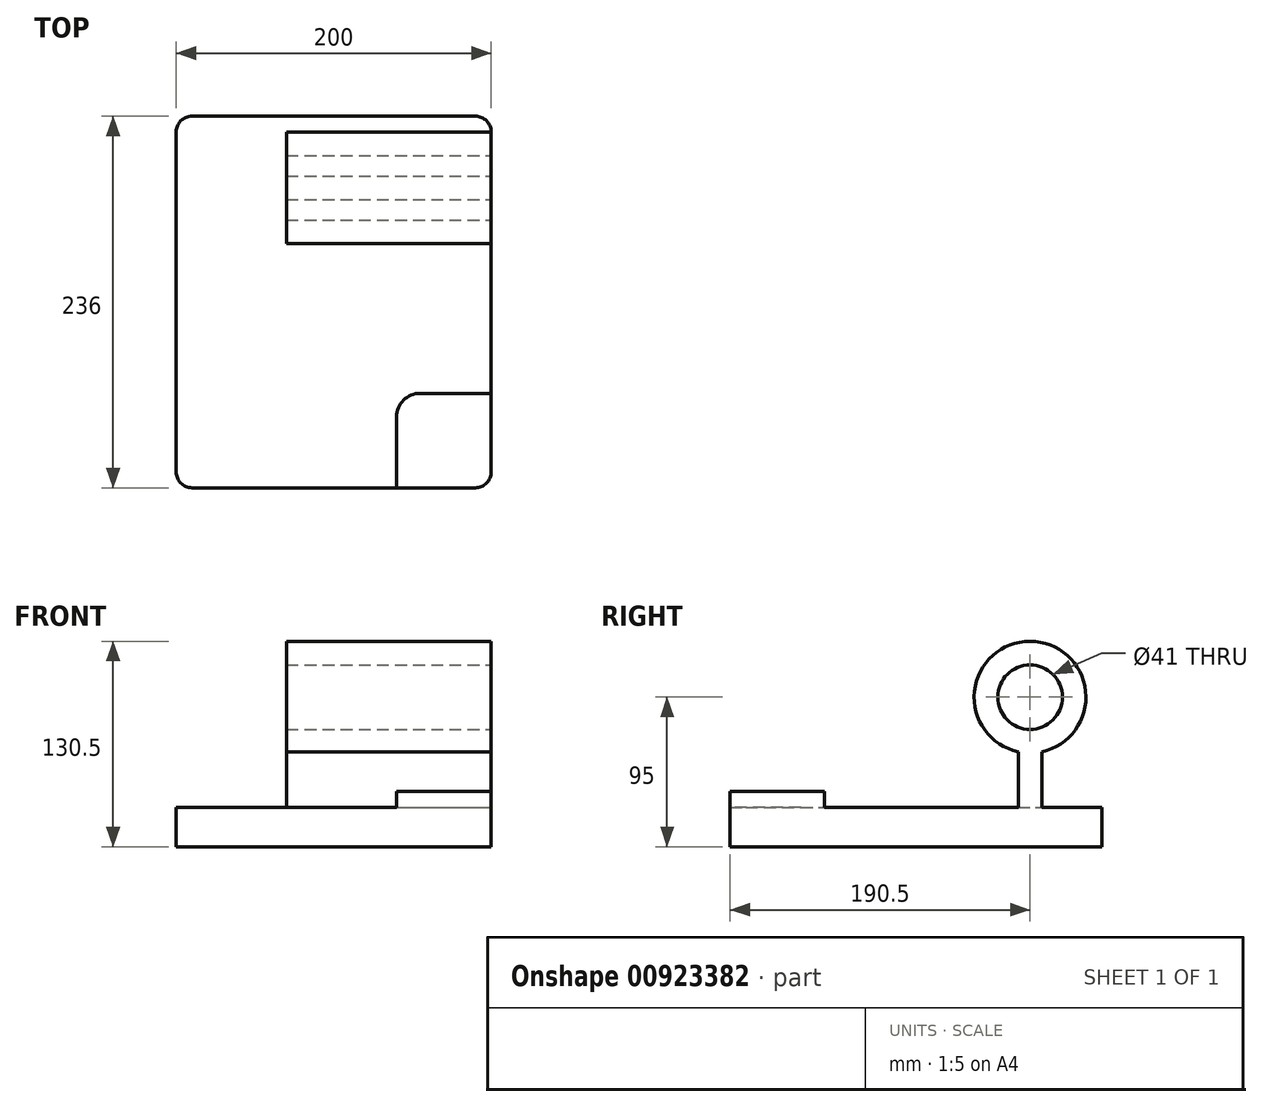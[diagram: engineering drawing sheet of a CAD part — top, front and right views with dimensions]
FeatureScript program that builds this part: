
annotation { "Feature Type Name" : "Feature", "Feature Type Description" : "" }
export const myFeature = defineFeature(function(context is Context, id is Id, definition is map)
    precondition{}
    {
        {
            var Q0;
            Q0=qCreatedBy(makeId("Right.planeOp"),FACE);
            var sketch = newSketch(context, id + "F0", { "sketchPlane" : qUnion([Q0])});
            skLineSegment(sketch, "E0", {"start": v(0, 0) * mm, "end": v(60, 0) * mm});
            skLineSegment(sketch, "E1", {"start": v(60, 0) * mm, "end": v(60, -10) * mm});
            skLineSegment(sketch, "E2", {"start": v(60, -10) * mm, "end": v(183, -10) * mm});
            skLineSegment(sketch, "E3", {"start": v(183, -10) * mm, "end": v(183, 25.3) * mm});
            skLineSegment(sketch, "E4", {"start": v(198, 25.3) * mm, "end": v(198, -10) * mm});
            skLineSegment(sketch, "E5", {"start": v(198, -10) * mm, "end": v(236, -10) * mm});
            skLineSegment(sketch, "E6", {"start": v(236, -10) * mm, "end": v(236, -35) * mm});
            skLineSegment(sketch, "E7", {"start": v(236, -35) * mm, "end": v(0, -35) * mm});
            skLineSegment(sketch, "E8", {"start": v(0, -35) * mm, "end": v(0, 0) * mm});
            skCircle(sketch, "E9", {"center": v(190.5, 60) * mm, "radius": 35.5 * mm});
            skCircle(sketch, "E10", {"center": v(190.5, 60) * mm, "radius": 20.5 * mm});
            skPoint(sketch, "E11.orphan", {"position": v(183, 60) * mm});
            skPoint(sketch, "E12.orphan", {"position": v(198, 60) * mm});
            skLineSegment(sketch, "E13", {"start": v(60, -10) * mm, "end": v(0, -10) * mm});
            skLineSegment(sketch, "E14", {"start": v(183, -10) * mm, "end": v(198, -10) * mm});
            skSolve(sketch);
        }
        {
            var Q0;
            Q0=makeQuery(id+"F0.imprint","IMPRINT",FACE,{"disambiguationData":[TD([[makeQuery(id+"F0.imprint","IMPRINT",EDGE,{"derivedFrom":sQuery(id+"F0.wireOp",EDGE,"E2")}),-1.0]])]});
            extrude(context, id + "F1", {"entities" : qUnion([Q0]), "oppositeDirection" : true, "depth" : 200 * mm, "offsetDistance" : 25 * mm});
        }
        {
            var Q0;
            {var subQ0=sQuery(id+"F0.wireOp",EDGE,"E0");Q0=makeQuery(id+"F0.imprint","IMPRINT",FACE,{"disambiguationData":[TD([[makeQuery(id+"F0.imprint","IMPRINT",EDGE,{"derivedFrom":subQ0}),-1.0]])]});}
            extrude(context, id + "F2", {"entities" : qUnion([Q0]), "operationType" : NewBodyOperationType.ADD, "oppositeDirection" : true, "depth" : 60 * mm, "offsetDistance" : 25 * mm});
        }
        {
            var Q0;
            Q0=makeQuery(id+"F0.imprint","IMPRINT",FACE,{"disambiguationData":[TD([[makeQuery(id+"F0.imprint","IMPRINT",EDGE,{"derivedFrom":sQuery(id+"F0.wireOp",EDGE,"E10")}),-1.0]])]});
            var Q1;
            {var subQ0=sQuery(id+"F0.wireOp",EDGE,"E3");Q1=makeQuery(id+"F0.imprint","IMPRINT",FACE,{"disambiguationData":[TD([[makeQuery(id+"F0.imprint","IMPRINT",EDGE,{"derivedFrom":subQ0}),-1.0]])]});}
            extrude(context, id + "F3", {"entities" : qUnion([Q0, Q1]), "operationType" : NewBodyOperationType.ADD, "oppositeDirection" : true, "depth" : 130 * mm, "offsetDistance" : 25 * mm});
        }
        {
            var Q0;
            {var subQ0=sQuery(id+"F0.wireOp",EDGE,"E8");Q0=makeQuery(id+"F2.boolean.opBoolean","MERGE",EDGE,{"derivedFrom":[makeQuery(id+"F1.opExtrude","CAP_EDGE",EDGE,{"disambiguationData":[OSD([subQ0])],"isStart":true}),makeQuery(id+"F2.opExtrude","CAP_EDGE",EDGE,{"disambiguationData":[OSD([subQ0])],"isStart":true})]});}
            var Q1;
            Q1=makeQuery(id+"F1.opExtrude","CAP_EDGE",EDGE,{"disambiguationData":[OSD([sQuery(id+"F0.wireOp",EDGE,"E8")])],"isStart":false});
            var Q2;
            Q2=makeQuery(id+"F1.opExtrude","CAP_EDGE",EDGE,{"disambiguationData":[OSD([sQuery(id+"F0.wireOp",EDGE,"E6")])],"isStart":true});
            var Q3;
            Q3=makeQuery(id+"F1.opExtrude","CAP_EDGE",EDGE,{"disambiguationData":[OSD([sQuery(id+"F0.wireOp",EDGE,"E6")])],"isStart":false});
            fillet(context, id + "F4", {"entities" : qUnion([Q0, Q1, Q2, Q3]), "radius" : 10 * mm, "tangentPropagation" : true, "allowEdgeOverflow" : false});
        }
        {
            var Q0;
            Q0=makeQuery(id+"F2.opExtrude","CAP_EDGE",EDGE,{"disambiguationData":[OSD([sQuery(id+"F0.wireOp",EDGE,"E1")])],"isStart":false});
            fillet(context, id + "F5", {"entities" : qUnion([Q0]), "radius" : 15 * mm, "tangentPropagation" : true, "allowEdgeOverflow" : false});
        }
    });
